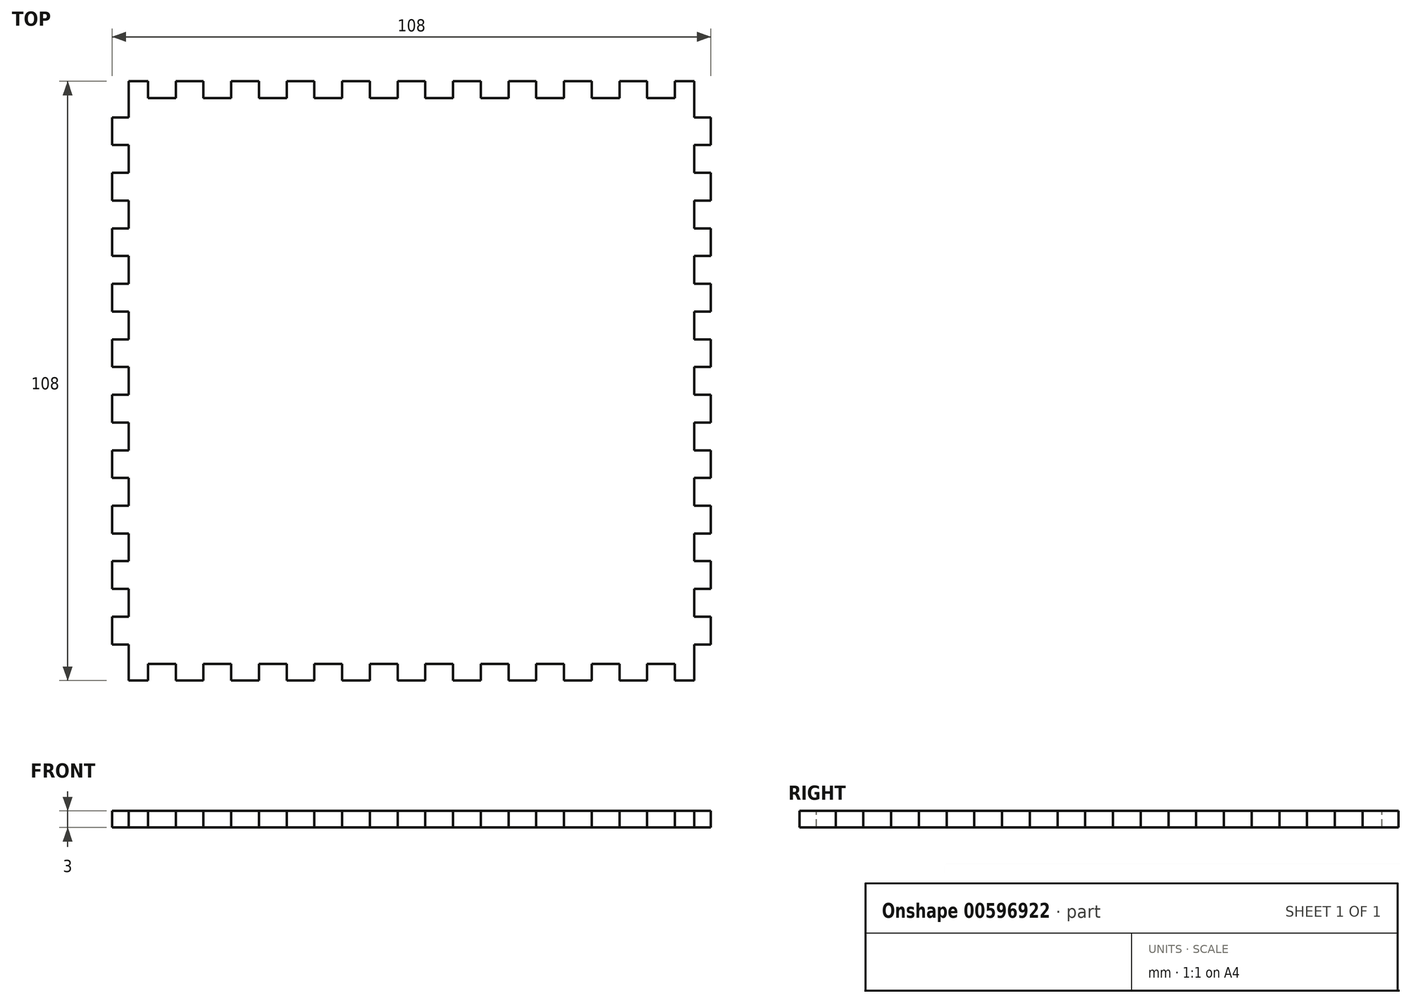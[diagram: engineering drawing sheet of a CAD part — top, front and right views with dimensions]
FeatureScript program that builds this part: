
annotation { "Feature Type Name" : "Feature", "Feature Type Description" : "" }
export const myFeature = defineFeature(function(context is Context, id is Id, definition is map)
    precondition{}
    {
        {
            var Q0;
            Q0=qCreatedBy(makeId("Top.planeOp"),FACE);
            var sketch = newSketch(context, id + "F0", { "sketchPlane" : qUnion([Q0])});
            skLineSegment(sketch, "E0.bottom", {"start": v(51, 51) * mm, "end": v(-51, 51) * mm});
            skLineSegment(sketch, "E0.top", {"start": v(51, -51) * mm, "end": v(-51, -51) * mm});
            skLineSegment(sketch, "E0.left", {"start": v(51, 51) * mm, "end": v(51, -51) * mm});
            skLineSegment(sketch, "E0.right", {"start": v(-51, 51) * mm, "end": v(-51, -51) * mm});
            skPoint(sketch, "E0.middle", {"position": v(0, 0) * mm});
            skSolve(sketch);
        }
        {
            var Q0;
            Q0 = qSketchRegion(id + "F0", true);
            extrude(context, id + "F1", {"entities" : qUnion([Q0]), "depth" : 3 * mm, "offsetDistance" : 25 * mm});
        }
        {
            var Q0;
            Q0=makeQuery(id+"F1.opExtrude","CAP_FACE",FACE,{"disambiguationData":[OSD([sQuery(id+"F0.wireOp",EDGE,"E0.bottom"),sQuery(id+"F0.wireOp",EDGE,"E0.top"),sQuery(id+"F0.wireOp",EDGE,"E0.left"),sQuery(id+"F0.wireOp",EDGE,"E0.right")])],"isStart":false});
            var sketch = newSketch(context, id + "F2", { "sketchPlane" : qUnion([Q0])});
            skLineSegment(sketch, "E1", {"start": v(0, 51) * mm, "end": v(0, 52.5) * mm, "construction": true});
            skPoint(sketch, "E1.endSnap0", {"position": v(0, 51) * mm});
            skLineSegment(sketch, "E2.bottom", {"start": v(2.5, 51) * mm, "end": v(-2.5, 51) * mm});
            skLineSegment(sketch, "E2.top", {"start": v(2.5, 54) * mm, "end": v(-2.5, 54) * mm});
            skLineSegment(sketch, "E2.left", {"start": v(2.5, 51) * mm, "end": v(2.5, 54) * mm});
            skLineSegment(sketch, "E2.right", {"start": v(-2.5, 51) * mm, "end": v(-2.5, 54) * mm});
            skPoint(sketch, "E2.middle", {"position": v(0, 52.5) * mm});
            skLineSegment(sketch, "E3.1.0.0", {"start": v(12.5, 54) * mm, "end": v(7.5, 54) * mm});
            skLineSegment(sketch, "E3.1.0.1", {"start": v(7.5, 51) * mm, "end": v(7.5, 54) * mm});
            skLineSegment(sketch, "E3.1.0.2", {"start": v(12.5, 51) * mm, "end": v(12.5, 54) * mm});
            skLineSegment(sketch, "E3.1.0.3", {"start": v(12.5, 51) * mm, "end": v(7.5, 51) * mm});
            skLineSegment(sketch, "E3.2.0.0", {"start": v(22.5, 54) * mm, "end": v(17.5, 54) * mm});
            skLineSegment(sketch, "E3.2.0.1", {"start": v(17.5, 51) * mm, "end": v(17.5, 54) * mm});
            skLineSegment(sketch, "E3.2.0.2", {"start": v(22.5, 51) * mm, "end": v(22.5, 54) * mm});
            skLineSegment(sketch, "E3.2.0.3", {"start": v(22.5, 51) * mm, "end": v(17.5, 51) * mm});
            skLineSegment(sketch, "E3.3.0.0", {"start": v(32.5, 54) * mm, "end": v(27.5, 54) * mm});
            skLineSegment(sketch, "E3.3.0.1", {"start": v(27.5, 51) * mm, "end": v(27.5, 54) * mm});
            skLineSegment(sketch, "E3.3.0.2", {"start": v(32.5, 51) * mm, "end": v(32.5, 54) * mm});
            skLineSegment(sketch, "E3.3.0.3", {"start": v(32.5, 51) * mm, "end": v(27.5, 51) * mm});
            skLineSegment(sketch, "E3.4.0.0", {"start": v(42.5, 54) * mm, "end": v(37.5, 54) * mm});
            skLineSegment(sketch, "E3.4.0.1", {"start": v(37.5, 51) * mm, "end": v(37.5, 54) * mm});
            skLineSegment(sketch, "E3.4.0.2", {"start": v(42.5, 51) * mm, "end": v(42.5, 54) * mm});
            skLineSegment(sketch, "E3.4.0.3", {"start": v(42.5, 51) * mm, "end": v(37.5, 51) * mm});
            skLineSegment(sketch, "E3.direction1", {"start": v(-2.5, 54) * mm, "end": v(7.5, 54) * mm, "construction": true});
            skLineSegment(sketch, "E4.MirrorCS", {"start": v(-12.5, 51) * mm, "end": v(-7.5, 51) * mm});
            skLineSegment(sketch, "E5.MirrorCS", {"start": v(-7.5, 51) * mm, "end": v(-7.5, 54) * mm});
            skLineSegment(sketch, "E6.MirrorCS", {"start": v(-12.5, 54) * mm, "end": v(-7.5, 54) * mm});
            skLineSegment(sketch, "E7.MirrorCS", {"start": v(-32.5, 51) * mm, "end": v(-32.5, 54) * mm});
            skLineSegment(sketch, "E8.MirrorCS", {"start": v(-27.5, 51) * mm, "end": v(-27.5, 54) * mm});
            skLineSegment(sketch, "E9.MirrorCS", {"start": v(-32.5, 54) * mm, "end": v(-27.5, 54) * mm});
            skLineSegment(sketch, "E10.MirrorCS", {"start": v(-42.5, 54) * mm, "end": v(-37.5, 54) * mm});
            skLineSegment(sketch, "E11.MirrorCS", {"start": v(-42.5, 51) * mm, "end": v(-42.5, 54) * mm});
            skLineSegment(sketch, "E12.MirrorCS", {"start": v(-32.5, 51) * mm, "end": v(-27.5, 51) * mm});
            skLineSegment(sketch, "E13.MirrorCS", {"start": v(-37.5, 51) * mm, "end": v(-37.5, 54) * mm});
            skLineSegment(sketch, "E14.MirrorCS", {"start": v(-42.5, 51) * mm, "end": v(-37.5, 51) * mm});
            skLineSegment(sketch, "E15.MirrorCS", {"start": v(-22.5, 51) * mm, "end": v(-17.5, 51) * mm});
            skLineSegment(sketch, "E16.MirrorCS", {"start": v(-22.5, 51) * mm, "end": v(-22.5, 54) * mm});
            skLineSegment(sketch, "E17.MirrorCS", {"start": v(-17.5, 51) * mm, "end": v(-17.5, 54) * mm});
            skLineSegment(sketch, "E18.MirrorCS", {"start": v(-22.5, 54) * mm, "end": v(-17.5, 54) * mm});
            skLineSegment(sketch, "E19.MirrorCS", {"start": v(-12.5, 51) * mm, "end": v(-12.5, 54) * mm});
            skLineSegment(sketch, "E20.MirrorCS", {"start": v(-7.5, -51) * mm, "end": v(-7.5, -54) * mm});
            skLineSegment(sketch, "E21.MirrorCS", {"start": v(0, -51) * mm, "end": v(0, -52.5) * mm, "construction": true});
            skLineSegment(sketch, "E22.MirrorCS", {"start": v(2.5, -51) * mm, "end": v(-2.5, -51) * mm});
            skLineSegment(sketch, "E23.MirrorCS", {"start": v(2.5, -54) * mm, "end": v(-2.5, -54) * mm});
            skLineSegment(sketch, "E24.MirrorCS", {"start": v(2.5, -51) * mm, "end": v(2.5, -54) * mm});
            skLineSegment(sketch, "E25.MirrorCS", {"start": v(-2.5, -51) * mm, "end": v(-2.5, -54) * mm});
            skLineSegment(sketch, "E26.MirrorCS", {"start": v(7.5, -51) * mm, "end": v(7.5, -54) * mm});
            skLineSegment(sketch, "E27.MirrorCS", {"start": v(42.5, -51) * mm, "end": v(42.5, -54) * mm});
            skLineSegment(sketch, "E28.MirrorCS", {"start": v(-17.5, -51) * mm, "end": v(-17.5, -54) * mm});
            skLineSegment(sketch, "E29.MirrorCS", {"start": v(-27.5, -51) * mm, "end": v(-27.5, -54) * mm});
            skLineSegment(sketch, "E30.MirrorCS", {"start": v(37.5, -51) * mm, "end": v(37.5, -54) * mm});
            skLineSegment(sketch, "E31.MirrorCS", {"start": v(-22.5, -51) * mm, "end": v(-22.5, -54) * mm});
            skLineSegment(sketch, "E32.MirrorCS", {"start": v(-12.5, -51) * mm, "end": v(-7.5, -51) * mm});
            skLineSegment(sketch, "E33.MirrorCS", {"start": v(-37.5, -51) * mm, "end": v(-37.5, -54) * mm});
            skLineSegment(sketch, "E34.MirrorCS", {"start": v(22.5, -51) * mm, "end": v(17.5, -51) * mm});
            skLineSegment(sketch, "E35.MirrorCS", {"start": v(-32.5, -51) * mm, "end": v(-32.5, -54) * mm});
            skLineSegment(sketch, "E36.MirrorCS", {"start": v(22.5, -51) * mm, "end": v(22.5, -54) * mm});
            skLineSegment(sketch, "E37.MirrorCS", {"start": v(17.5, -51) * mm, "end": v(17.5, -54) * mm});
            skLineSegment(sketch, "E38.MirrorCS", {"start": v(22.5, -54) * mm, "end": v(17.5, -54) * mm});
            skLineSegment(sketch, "E39.MirrorCS", {"start": v(12.5, -51) * mm, "end": v(7.5, -51) * mm});
            skLineSegment(sketch, "E40.MirrorCS", {"start": v(12.5, -51) * mm, "end": v(12.5, -54) * mm});
            skLineSegment(sketch, "E41.MirrorCS", {"start": v(-32.5, -51) * mm, "end": v(-27.5, -51) * mm});
            skLineSegment(sketch, "E42.MirrorCS", {"start": v(-12.5, -51) * mm, "end": v(-12.5, -54) * mm});
            skLineSegment(sketch, "E43.MirrorCS", {"start": v(-2.5, -54) * mm, "end": v(7.5, -54) * mm, "construction": true});
            skLineSegment(sketch, "E44.MirrorCS", {"start": v(-22.5, -51) * mm, "end": v(-17.5, -51) * mm});
            skLineSegment(sketch, "E45.MirrorCS", {"start": v(42.5, -54) * mm, "end": v(37.5, -54) * mm});
            skLineSegment(sketch, "E46.MirrorCS", {"start": v(-32.5, -54) * mm, "end": v(-27.5, -54) * mm});
            skLineSegment(sketch, "E47.MirrorCS", {"start": v(32.5, -54) * mm, "end": v(27.5, -54) * mm});
            skLineSegment(sketch, "E48.MirrorCS", {"start": v(27.5, -51) * mm, "end": v(27.5, -54) * mm});
            skLineSegment(sketch, "E49.MirrorCS", {"start": v(-22.5, -54) * mm, "end": v(-17.5, -54) * mm});
            skLineSegment(sketch, "E50.MirrorCS", {"start": v(-42.5, -51) * mm, "end": v(-42.5, -54) * mm});
            skLineSegment(sketch, "E51.MirrorCS", {"start": v(32.5, -51) * mm, "end": v(32.5, -54) * mm});
            skLineSegment(sketch, "E52.MirrorCS", {"start": v(42.5, -51) * mm, "end": v(37.5, -51) * mm});
            skLineSegment(sketch, "E53.MirrorCS", {"start": v(12.5, -54) * mm, "end": v(7.5, -54) * mm});
            skLineSegment(sketch, "E54.MirrorCS", {"start": v(-42.5, -51) * mm, "end": v(-37.5, -51) * mm});
            skLineSegment(sketch, "E55.MirrorCS", {"start": v(32.5, -51) * mm, "end": v(27.5, -51) * mm});
            skLineSegment(sketch, "E56.MirrorCS", {"start": v(-42.5, -54) * mm, "end": v(-37.5, -54) * mm});
            skLineSegment(sketch, "E57.MirrorCS", {"start": v(-12.5, -54) * mm, "end": v(-7.5, -54) * mm});
            skPoint(sketch, "E58.MirrorP", {"position": v(0, -52.5) * mm});
            skPoint(sketch, "E59.MirrorP", {"position": v(0, -51) * mm});
            skLineSegment(sketch, "E60", {"start": v(-42.5, 51) * mm, "end": v(-47.5, 51) * mm, "construction": true});
            skLineSegment(sketch, "E61.bottom", {"start": v(-47.5, 51) * mm, "end": v(-51, 51) * mm});
            skLineSegment(sketch, "E61.top", {"start": v(-47.5, 54) * mm, "end": v(-51, 54) * mm});
            skLineSegment(sketch, "E61.left", {"start": v(-47.5, 51) * mm, "end": v(-47.5, 54) * mm});
            skLineSegment(sketch, "E61.right", {"start": v(-51, 51) * mm, "end": v(-51, 54) * mm});
            skLineSegment(sketch, "E62.MirrorCS", {"start": v(47.5, 51) * mm, "end": v(51, 51) * mm});
            skLineSegment(sketch, "E63.MirrorCS", {"start": v(47.5, 54) * mm, "end": v(51, 54) * mm});
            skLineSegment(sketch, "E64.MirrorCS", {"start": v(47.5, 51) * mm, "end": v(47.5, 54) * mm});
            skLineSegment(sketch, "E65.MirrorCS", {"start": v(51, 51) * mm, "end": v(51, 54) * mm});
            skLineSegment(sketch, "E66.MirrorCS", {"start": v(51, -51) * mm, "end": v(51, -54) * mm});
            skLineSegment(sketch, "E67.MirrorCS", {"start": v(47.5, -51) * mm, "end": v(47.5, -54) * mm});
            skLineSegment(sketch, "E68.MirrorCS", {"start": v(47.5, -54) * mm, "end": v(51, -54) * mm});
            skLineSegment(sketch, "E69.MirrorCS", {"start": v(47.5, -51) * mm, "end": v(51, -51) * mm});
            skLineSegment(sketch, "E70.MirrorCS", {"start": v(-47.5, -51) * mm, "end": v(-51, -51) * mm});
            skLineSegment(sketch, "E71.MirrorCS", {"start": v(-47.5, -54) * mm, "end": v(-51, -54) * mm});
            skLineSegment(sketch, "E72.MirrorCS", {"start": v(-47.5, -51) * mm, "end": v(-47.5, -54) * mm});
            skLineSegment(sketch, "E73.MirrorCS", {"start": v(-51, -51) * mm, "end": v(-51, -54) * mm});
            skSolve(sketch);
        }
        {
            var Q0;
            Q0 = qSketchRegion(id + "F2", true);
            var Q1;
            Q1=makeQuery(id+"F1.opExtrude","CAP_FACE",FACE,{"disambiguationData":[OSD([sQuery(id+"F0.wireOp",EDGE,"E0.bottom"),sQuery(id+"F0.wireOp",EDGE,"E0.top"),sQuery(id+"F0.wireOp",EDGE,"E0.left"),sQuery(id+"F0.wireOp",EDGE,"E0.right")])],"isStart":true});
            extrude(context, id + "F3", {"entities" : qUnion([Q0]), "operationType" : NewBodyOperationType.ADD, "endBound" : BoundingType.UP_TO_SURFACE, "oppositeDirection" : true, "depth" : 25 * mm, "endBoundEntityFace" : qUnion([Q1]), "offsetDistance" : 25 * mm});
        }
        {
            var Q0;
            Q0=makeQuery(id+"F3.boolean.opBoolean","MERGE",FACE,{"derivedFrom":[makeQuery(id+"F1.opExtrude","CAP_FACE",FACE,{"disambiguationData":[OSD([sQuery(id+"F0.wireOp",EDGE,"E0.bottom"),sQuery(id+"F0.wireOp",EDGE,"E0.top"),sQuery(id+"F0.wireOp",EDGE,"E0.left"),sQuery(id+"F0.wireOp",EDGE,"E0.right")])],"isStart":false}),makeQuery(id+"F3.opExtrude","CAP_FACE",FACE,{"disambiguationData":[OSD([sQuery(id+"F2.wireOp",EDGE,"E2.bottom"),sQuery(id+"F2.wireOp",EDGE,"E2.top"),sQuery(id+"F2.wireOp",EDGE,"E2.left"),sQuery(id+"F2.wireOp",EDGE,"E2.right")])],"isStart":true}),makeQuery(id+"F3.opExtrude","CAP_FACE",FACE,{"disambiguationData":[OSD([sQuery(id+"F2.wireOp",EDGE,"E3.1.0.0"),sQuery(id+"F2.wireOp",EDGE,"E3.1.0.1"),sQuery(id+"F2.wireOp",EDGE,"E3.1.0.2"),sQuery(id+"F2.wireOp",EDGE,"E3.1.0.3")])],"isStart":true}),makeQuery(id+"F3.opExtrude","CAP_FACE",FACE,{"disambiguationData":[OSD([sQuery(id+"F2.wireOp",EDGE,"E3.2.0.0"),sQuery(id+"F2.wireOp",EDGE,"E3.2.0.1"),sQuery(id+"F2.wireOp",EDGE,"E3.2.0.2"),sQuery(id+"F2.wireOp",EDGE,"E3.2.0.3")])],"isStart":true}),makeQuery(id+"F3.opExtrude","CAP_FACE",FACE,{"disambiguationData":[OSD([sQuery(id+"F2.wireOp",EDGE,"E3.3.0.0"),sQuery(id+"F2.wireOp",EDGE,"E3.3.0.1"),sQuery(id+"F2.wireOp",EDGE,"E3.3.0.2"),sQuery(id+"F2.wireOp",EDGE,"E3.3.0.3")])],"isStart":true}),makeQuery(id+"F3.opExtrude","CAP_FACE",FACE,{"disambiguationData":[OSD([sQuery(id+"F2.wireOp",EDGE,"E3.4.0.0"),sQuery(id+"F2.wireOp",EDGE,"E3.4.0.1"),sQuery(id+"F2.wireOp",EDGE,"E3.4.0.2"),sQuery(id+"F2.wireOp",EDGE,"E3.4.0.3")])],"isStart":true}),makeQuery(id+"F3.opExtrude","CAP_FACE",FACE,{"disambiguationData":[OSD([sQuery(id+"F2.wireOp",EDGE,"E4.MirrorCS"),sQuery(id+"F2.wireOp",EDGE,"E5.MirrorCS"),sQuery(id+"F2.wireOp",EDGE,"E6.MirrorCS"),sQuery(id+"F2.wireOp",EDGE,"E19.MirrorCS")])],"isStart":true}),makeQuery(id+"F3.opExtrude","CAP_FACE",FACE,{"disambiguationData":[OSD([sQuery(id+"F2.wireOp",EDGE,"E7.MirrorCS"),sQuery(id+"F2.wireOp",EDGE,"E8.MirrorCS"),sQuery(id+"F2.wireOp",EDGE,"E9.MirrorCS"),sQuery(id+"F2.wireOp",EDGE,"E12.MirrorCS")])],"isStart":true}),makeQuery(id+"F3.opExtrude","CAP_FACE",FACE,{"disambiguationData":[OSD([sQuery(id+"F2.wireOp",EDGE,"E10.MirrorCS"),sQuery(id+"F2.wireOp",EDGE,"E11.MirrorCS"),sQuery(id+"F2.wireOp",EDGE,"E13.MirrorCS"),sQuery(id+"F2.wireOp",EDGE,"E14.MirrorCS")])],"isStart":true}),makeQuery(id+"F3.opExtrude","CAP_FACE",FACE,{"disambiguationData":[OSD([sQuery(id+"F2.wireOp",EDGE,"E15.MirrorCS"),sQuery(id+"F2.wireOp",EDGE,"E16.MirrorCS"),sQuery(id+"F2.wireOp",EDGE,"E17.MirrorCS"),sQuery(id+"F2.wireOp",EDGE,"E18.MirrorCS")])],"isStart":true}),makeQuery(id+"F3.opExtrude","CAP_FACE",FACE,{"disambiguationData":[OSD([sQuery(id+"F2.wireOp",EDGE,"E20.MirrorCS"),sQuery(id+"F2.wireOp",EDGE,"E32.MirrorCS"),sQuery(id+"F2.wireOp",EDGE,"E42.MirrorCS"),sQuery(id+"F2.wireOp",EDGE,"E57.MirrorCS")])],"isStart":true}),makeQuery(id+"F3.opExtrude","CAP_FACE",FACE,{"disambiguationData":[OSD([sQuery(id+"F2.wireOp",EDGE,"E22.MirrorCS"),sQuery(id+"F2.wireOp",EDGE,"E23.MirrorCS"),sQuery(id+"F2.wireOp",EDGE,"E24.MirrorCS"),sQuery(id+"F2.wireOp",EDGE,"E25.MirrorCS")])],"isStart":true}),makeQuery(id+"F3.opExtrude","CAP_FACE",FACE,{"disambiguationData":[OSD([sQuery(id+"F2.wireOp",EDGE,"E26.MirrorCS"),sQuery(id+"F2.wireOp",EDGE,"E39.MirrorCS"),sQuery(id+"F2.wireOp",EDGE,"E40.MirrorCS"),sQuery(id+"F2.wireOp",EDGE,"E53.MirrorCS")])],"isStart":true}),makeQuery(id+"F3.opExtrude","CAP_FACE",FACE,{"disambiguationData":[OSD([sQuery(id+"F2.wireOp",EDGE,"E27.MirrorCS"),sQuery(id+"F2.wireOp",EDGE,"E30.MirrorCS"),sQuery(id+"F2.wireOp",EDGE,"E45.MirrorCS"),sQuery(id+"F2.wireOp",EDGE,"E52.MirrorCS")])],"isStart":true}),makeQuery(id+"F3.opExtrude","CAP_FACE",FACE,{"disambiguationData":[OSD([sQuery(id+"F2.wireOp",EDGE,"E28.MirrorCS"),sQuery(id+"F2.wireOp",EDGE,"E31.MirrorCS"),sQuery(id+"F2.wireOp",EDGE,"E44.MirrorCS"),sQuery(id+"F2.wireOp",EDGE,"E49.MirrorCS")])],"isStart":true}),makeQuery(id+"F3.opExtrude","CAP_FACE",FACE,{"disambiguationData":[OSD([sQuery(id+"F2.wireOp",EDGE,"E29.MirrorCS"),sQuery(id+"F2.wireOp",EDGE,"E35.MirrorCS"),sQuery(id+"F2.wireOp",EDGE,"E41.MirrorCS"),sQuery(id+"F2.wireOp",EDGE,"E46.MirrorCS")])],"isStart":true}),makeQuery(id+"F3.opExtrude","CAP_FACE",FACE,{"disambiguationData":[OSD([sQuery(id+"F2.wireOp",EDGE,"E33.MirrorCS"),sQuery(id+"F2.wireOp",EDGE,"E50.MirrorCS"),sQuery(id+"F2.wireOp",EDGE,"E54.MirrorCS"),sQuery(id+"F2.wireOp",EDGE,"E56.MirrorCS")])],"isStart":true}),makeQuery(id+"F3.opExtrude","CAP_FACE",FACE,{"disambiguationData":[OSD([sQuery(id+"F2.wireOp",EDGE,"E34.MirrorCS"),sQuery(id+"F2.wireOp",EDGE,"E36.MirrorCS"),sQuery(id+"F2.wireOp",EDGE,"E37.MirrorCS"),sQuery(id+"F2.wireOp",EDGE,"E38.MirrorCS")])],"isStart":true}),makeQuery(id+"F3.opExtrude","CAP_FACE",FACE,{"disambiguationData":[OSD([sQuery(id+"F2.wireOp",EDGE,"E47.MirrorCS"),sQuery(id+"F2.wireOp",EDGE,"E48.MirrorCS"),sQuery(id+"F2.wireOp",EDGE,"E51.MirrorCS"),sQuery(id+"F2.wireOp",EDGE,"E55.MirrorCS")])],"isStart":true}),makeQuery(id+"F3.opExtrude","CAP_FACE",FACE,{"disambiguationData":[OSD([sQuery(id+"F2.wireOp",EDGE,"E61.bottom"),sQuery(id+"F2.wireOp",EDGE,"E61.top"),sQuery(id+"F2.wireOp",EDGE,"E61.left"),sQuery(id+"F2.wireOp",EDGE,"E61.right")])],"isStart":true}),makeQuery(id+"F3.opExtrude","CAP_FACE",FACE,{"disambiguationData":[OSD([sQuery(id+"F2.wireOp",EDGE,"E62.MirrorCS"),sQuery(id+"F2.wireOp",EDGE,"E63.MirrorCS"),sQuery(id+"F2.wireOp",EDGE,"E64.MirrorCS"),sQuery(id+"F2.wireOp",EDGE,"E65.MirrorCS")])],"isStart":true}),makeQuery(id+"F3.opExtrude","CAP_FACE",FACE,{"disambiguationData":[OSD([sQuery(id+"F2.wireOp",EDGE,"E66.MirrorCS"),sQuery(id+"F2.wireOp",EDGE,"E67.MirrorCS"),sQuery(id+"F2.wireOp",EDGE,"E68.MirrorCS"),sQuery(id+"F2.wireOp",EDGE,"E69.MirrorCS")])],"isStart":true}),makeQuery(id+"F3.opExtrude","CAP_FACE",FACE,{"disambiguationData":[OSD([sQuery(id+"F2.wireOp",EDGE,"E70.MirrorCS"),sQuery(id+"F2.wireOp",EDGE,"E71.MirrorCS"),sQuery(id+"F2.wireOp",EDGE,"E72.MirrorCS"),sQuery(id+"F2.wireOp",EDGE,"E73.MirrorCS")])],"isStart":true})]});
            var sketch = newSketch(context, id + "F4", { "sketchPlane" : qUnion([Q0])});
            skLineSegment(sketch, "E74", {"start": v(51, 0) * mm, "end": v(51, -2.5) * mm, "construction": true});
            skLineSegment(sketch, "E75.bottom", {"start": v(51, -2.5) * mm, "end": v(54, -2.5) * mm});
            skLineSegment(sketch, "E75.top", {"start": v(51, -7.5) * mm, "end": v(54, -7.5) * mm});
            skLineSegment(sketch, "E75.left", {"start": v(51, -2.5) * mm, "end": v(51, -7.5) * mm});
            skLineSegment(sketch, "E75.right", {"start": v(54, -2.5) * mm, "end": v(54, -7.5) * mm});
            skLineSegment(sketch, "E76.0.1.0", {"start": v(54, -12.5) * mm, "end": v(54, -17.5) * mm});
            skLineSegment(sketch, "E76.0.1.1", {"start": v(51, -12.5) * mm, "end": v(54, -12.5) * mm});
            skLineSegment(sketch, "E76.0.1.2", {"start": v(51, -17.5) * mm, "end": v(54, -17.5) * mm});
            skLineSegment(sketch, "E76.0.1.3", {"start": v(51, -12.5) * mm, "end": v(51, -17.5) * mm});
            skLineSegment(sketch, "E76.0.2.0", {"start": v(54, -22.5) * mm, "end": v(54, -27.5) * mm});
            skLineSegment(sketch, "E76.0.2.1", {"start": v(51, -22.5) * mm, "end": v(54, -22.5) * mm});
            skLineSegment(sketch, "E76.0.2.2", {"start": v(51, -27.5) * mm, "end": v(54, -27.5) * mm});
            skLineSegment(sketch, "E76.0.2.3", {"start": v(51, -22.5) * mm, "end": v(51, -27.5) * mm});
            skLineSegment(sketch, "E76.0.3.0", {"start": v(54, -32.5) * mm, "end": v(54, -37.5) * mm});
            skLineSegment(sketch, "E76.0.3.1", {"start": v(51, -32.5) * mm, "end": v(54, -32.5) * mm});
            skLineSegment(sketch, "E76.0.3.2", {"start": v(51, -37.5) * mm, "end": v(54, -37.5) * mm});
            skLineSegment(sketch, "E76.0.3.3", {"start": v(51, -32.5) * mm, "end": v(51, -37.5) * mm});
            skLineSegment(sketch, "E76.0.4.0", {"start": v(54, -42.5) * mm, "end": v(54, -47.5) * mm});
            skLineSegment(sketch, "E76.0.4.1", {"start": v(51, -42.5) * mm, "end": v(54, -42.5) * mm});
            skLineSegment(sketch, "E76.0.4.2", {"start": v(51, -47.5) * mm, "end": v(54, -47.5) * mm});
            skLineSegment(sketch, "E76.0.4.3", {"start": v(51, -42.5) * mm, "end": v(51, -47.5) * mm});
            skLineSegment(sketch, "E76.direction1", {"start": v(54, -7.5) * mm, "end": v(79, -7.5) * mm, "construction": true});
            skLineSegment(sketch, "E76.direction2", {"start": v(54, -7.5) * mm, "end": v(54, -17.5) * mm, "construction": true});
            skLineSegment(sketch, "E77.MirrorCS", {"start": v(54, 12.5) * mm, "end": v(54, 17.5) * mm});
            skLineSegment(sketch, "E78.MirrorCS", {"start": v(54, 42.5) * mm, "end": v(54, 47.5) * mm});
            skLineSegment(sketch, "E79.MirrorCS", {"start": v(51, 22.5) * mm, "end": v(51, 27.5) * mm});
            skLineSegment(sketch, "E80.MirrorCS", {"start": v(51, 27.5) * mm, "end": v(54, 27.5) * mm});
            skLineSegment(sketch, "E81.MirrorCS", {"start": v(51, 22.5) * mm, "end": v(54, 22.5) * mm});
            skLineSegment(sketch, "E82.MirrorCS", {"start": v(54, 22.5) * mm, "end": v(54, 27.5) * mm});
            skLineSegment(sketch, "E83.MirrorCS", {"start": v(51, 12.5) * mm, "end": v(51, 17.5) * mm});
            skLineSegment(sketch, "E84.MirrorCS", {"start": v(51, 17.5) * mm, "end": v(54, 17.5) * mm});
            skLineSegment(sketch, "E85.MirrorCS", {"start": v(51, 12.5) * mm, "end": v(54, 12.5) * mm});
            skLineSegment(sketch, "E86.MirrorCS", {"start": v(54, 2.5) * mm, "end": v(54, 7.5) * mm});
            skLineSegment(sketch, "E87.MirrorCS", {"start": v(51, 2.5) * mm, "end": v(51, 7.5) * mm});
            skLineSegment(sketch, "E88.MirrorCS", {"start": v(51, 7.5) * mm, "end": v(54, 7.5) * mm});
            skLineSegment(sketch, "E89.MirrorCS", {"start": v(51, 2.5) * mm, "end": v(54, 2.5) * mm});
            skLineSegment(sketch, "E90.MirrorCS", {"start": v(51, 37.5) * mm, "end": v(54, 37.5) * mm});
            skLineSegment(sketch, "E91.MirrorCS", {"start": v(51, 32.5) * mm, "end": v(54, 32.5) * mm});
            skLineSegment(sketch, "E92.MirrorCS", {"start": v(54, 32.5) * mm, "end": v(54, 37.5) * mm});
            skLineSegment(sketch, "E93.MirrorCS", {"start": v(51, 42.5) * mm, "end": v(51, 47.5) * mm});
            skLineSegment(sketch, "E94.MirrorCS", {"start": v(54, 7.5) * mm, "end": v(54, 17.5) * mm, "construction": true});
            skLineSegment(sketch, "E95.MirrorCS", {"start": v(51, 42.5) * mm, "end": v(54, 42.5) * mm});
            skLineSegment(sketch, "E96.MirrorCS", {"start": v(51, 47.5) * mm, "end": v(54, 47.5) * mm});
            skLineSegment(sketch, "E97.MirrorCS", {"start": v(51, 32.5) * mm, "end": v(51, 37.5) * mm});
            skLineSegment(sketch, "E98.MirrorCS", {"start": v(-54, -12.5) * mm, "end": v(-54, -17.5) * mm});
            skLineSegment(sketch, "E99.MirrorCS", {"start": v(-51, -2.5) * mm, "end": v(-54, -2.5) * mm});
            skLineSegment(sketch, "E100.MirrorCS", {"start": v(-51, 0) * mm, "end": v(-51, -2.5) * mm, "construction": true});
            skLineSegment(sketch, "E101.MirrorCS", {"start": v(-51, 17.5) * mm, "end": v(-54, 17.5) * mm});
            skLineSegment(sketch, "E102.MirrorCS", {"start": v(-51, 32.5) * mm, "end": v(-54, 32.5) * mm});
            skLineSegment(sketch, "E103.MirrorCS", {"start": v(-51, -22.5) * mm, "end": v(-51, -27.5) * mm});
            skLineSegment(sketch, "E104.MirrorCS", {"start": v(-51, -27.5) * mm, "end": v(-54, -27.5) * mm});
            skLineSegment(sketch, "E105.MirrorCS", {"start": v(-54, 22.5) * mm, "end": v(-54, 27.5) * mm});
            skLineSegment(sketch, "E106.MirrorCS", {"start": v(-51, -22.5) * mm, "end": v(-54, -22.5) * mm});
            skLineSegment(sketch, "E107.MirrorCS", {"start": v(-54, -22.5) * mm, "end": v(-54, -27.5) * mm});
            skLineSegment(sketch, "E108.MirrorCS", {"start": v(-51, -12.5) * mm, "end": v(-51, -17.5) * mm});
            skLineSegment(sketch, "E109.MirrorCS", {"start": v(-51, -17.5) * mm, "end": v(-54, -17.5) * mm});
            skLineSegment(sketch, "E110.MirrorCS", {"start": v(-51, -12.5) * mm, "end": v(-54, -12.5) * mm});
            skLineSegment(sketch, "E111.MirrorCS", {"start": v(-54, -2.5) * mm, "end": v(-54, -7.5) * mm});
            skLineSegment(sketch, "E112.MirrorCS", {"start": v(-51, -2.5) * mm, "end": v(-51, -7.5) * mm});
            skLineSegment(sketch, "E113.MirrorCS", {"start": v(-51, -7.5) * mm, "end": v(-54, -7.5) * mm});
            skLineSegment(sketch, "E114.MirrorCS", {"start": v(-51, -37.5) * mm, "end": v(-54, -37.5) * mm});
            skLineSegment(sketch, "E115.MirrorCS", {"start": v(-51, -32.5) * mm, "end": v(-54, -32.5) * mm});
            skLineSegment(sketch, "E116.MirrorCS", {"start": v(-54, -32.5) * mm, "end": v(-54, -37.5) * mm});
            skLineSegment(sketch, "E117.MirrorCS", {"start": v(-51, 12.5) * mm, "end": v(-54, 12.5) * mm});
            skLineSegment(sketch, "E118.MirrorCS", {"start": v(-54, 32.5) * mm, "end": v(-54, 37.5) * mm});
            skLineSegment(sketch, "E119.MirrorCS", {"start": v(-54, -7.5) * mm, "end": v(-54, -17.5) * mm, "construction": true});
            skLineSegment(sketch, "E120.MirrorCS", {"start": v(-51, 32.5) * mm, "end": v(-51, 37.5) * mm});
            skLineSegment(sketch, "E121.MirrorCS", {"start": v(-51, -32.5) * mm, "end": v(-51, -37.5) * mm});
            skLineSegment(sketch, "E122.MirrorCS", {"start": v(-51, 42.5) * mm, "end": v(-51, 47.5) * mm});
            skLineSegment(sketch, "E123.MirrorCS", {"start": v(-54, 12.5) * mm, "end": v(-54, 17.5) * mm});
            skLineSegment(sketch, "E124.MirrorCS", {"start": v(-54, 7.5) * mm, "end": v(-54, 17.5) * mm, "construction": true});
            skLineSegment(sketch, "E125.MirrorCS", {"start": v(-54, 42.5) * mm, "end": v(-54, 47.5) * mm});
            skLineSegment(sketch, "E126.MirrorCS", {"start": v(-54, -42.5) * mm, "end": v(-54, -47.5) * mm});
            skLineSegment(sketch, "E127.MirrorCS", {"start": v(-51, 42.5) * mm, "end": v(-54, 42.5) * mm});
            skLineSegment(sketch, "E128.MirrorCS", {"start": v(-51, 22.5) * mm, "end": v(-54, 22.5) * mm});
            skLineSegment(sketch, "E129.MirrorCS", {"start": v(-51, 22.5) * mm, "end": v(-51, 27.5) * mm});
            skLineSegment(sketch, "E130.MirrorCS", {"start": v(-51, -42.5) * mm, "end": v(-54, -42.5) * mm});
            skLineSegment(sketch, "E131.MirrorCS", {"start": v(-51, 7.5) * mm, "end": v(-54, 7.5) * mm});
            skLineSegment(sketch, "E132.MirrorCS", {"start": v(-51, 37.5) * mm, "end": v(-54, 37.5) * mm});
            skLineSegment(sketch, "E133.MirrorCS", {"start": v(-51, -47.5) * mm, "end": v(-54, -47.5) * mm});
            skLineSegment(sketch, "E134.MirrorCS", {"start": v(-51, 2.5) * mm, "end": v(-54, 2.5) * mm});
            skLineSegment(sketch, "E135.MirrorCS", {"start": v(-51, 47.5) * mm, "end": v(-54, 47.5) * mm});
            skLineSegment(sketch, "E136.MirrorCS", {"start": v(-51, 27.5) * mm, "end": v(-54, 27.5) * mm});
            skLineSegment(sketch, "E137.MirrorCS", {"start": v(-51, -42.5) * mm, "end": v(-51, -47.5) * mm});
            skLineSegment(sketch, "E138.MirrorCS", {"start": v(-51, 12.5) * mm, "end": v(-51, 17.5) * mm});
            skLineSegment(sketch, "E139.MirrorCS", {"start": v(-54, 2.5) * mm, "end": v(-54, 7.5) * mm});
            skLineSegment(sketch, "E140.MirrorCS", {"start": v(-51, 2.5) * mm, "end": v(-51, 7.5) * mm});
            skSolve(sketch);
        }
        {
            var Q0;
            Q0 = qSketchRegion(id + "F4", true);
            extrude(context, id + "F5", {"entities" : qUnion([Q0]), "operationType" : NewBodyOperationType.ADD, "oppositeDirection" : true, "depth" : 3 * mm, "offsetDistance" : 25 * mm});
        }
    });
